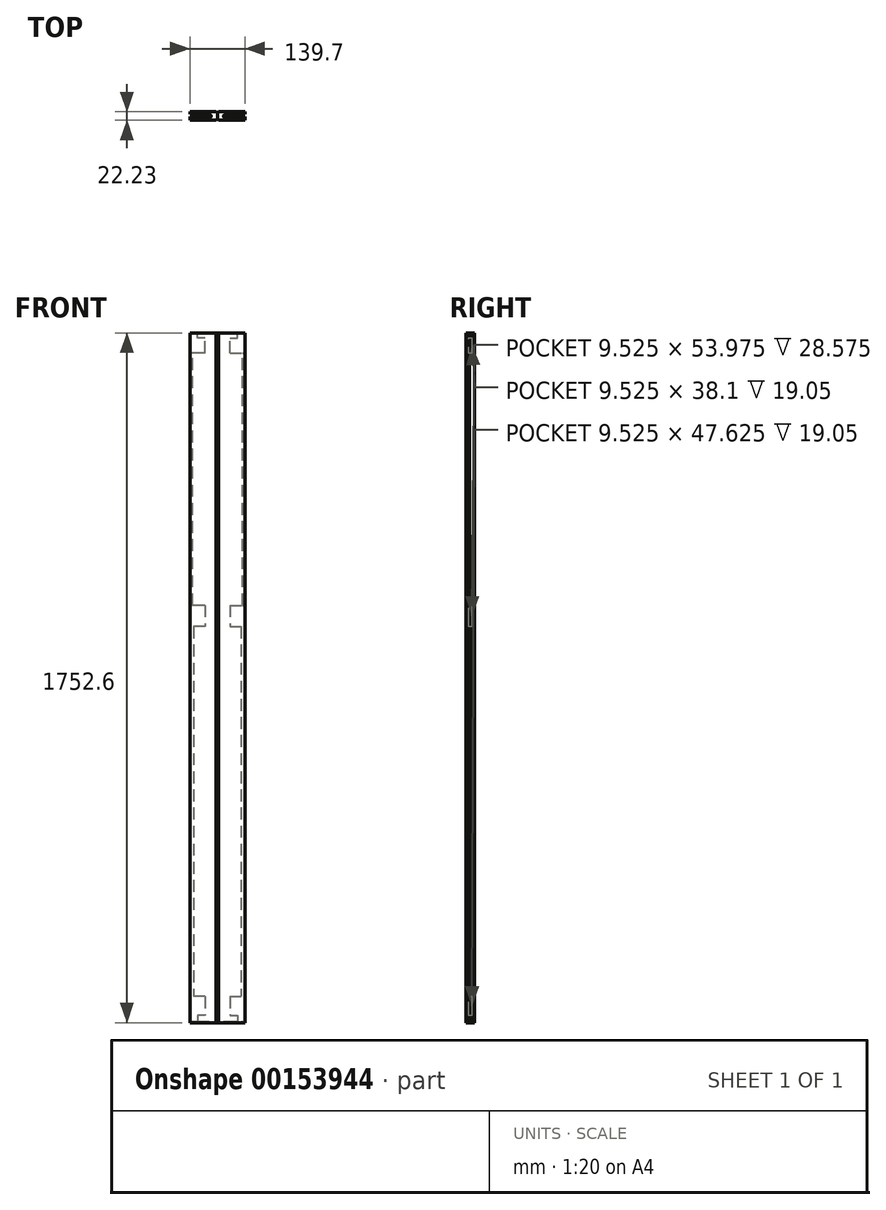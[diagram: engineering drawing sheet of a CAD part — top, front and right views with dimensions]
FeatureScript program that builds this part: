
annotation { "Feature Type Name" : "Feature", "Feature Type Description" : "" }
export const myFeature = defineFeature(function(context is Context, id is Id, definition is map)
    precondition{}
    {
        {
            var Q0;
            Q0=qCreatedBy(makeId("Front.planeOp"),FACE);
            var sketch = newSketch(context, id + "F0", { "sketchPlane" : qUnion([Q0])});
            skLineSegment(sketch, "E0.bottom", {"start": v(0, 0) * mm, "end": v(69.85, 0) * mm});
            skLineSegment(sketch, "E0.top", {"start": v(0, 1778) * mm, "end": v(69.85, 1778) * mm});
            skLineSegment(sketch, "E0.left", {"start": v(0, 0) * mm, "end": v(0, 1778) * mm});
            skLineSegment(sketch, "E0.right", {"start": v(69.85, 0) * mm, "end": v(69.85, 1778) * mm});
            skSolve(sketch);
        }
        {
            var Q0;
            Q0=makeQuery(id+"F0.imprint","IMPRINT",FACE,{"disambiguationData":[TD([[makeQuery(id+"F0.imprint","IMPRINT",EDGE,{"derivedFrom":sQuery(id+"F0.wireOp",EDGE,"E0.bottom")}),1.0]])]});
            extrude(context, id + "F1", {"entities" : qUnion([Q0]), "depth" : 22.22 * mm});
        }
        {
            var Q0;
            Q0=makeQuery(id+"F1.opExtrude","SWEPT_FACE",FACE,{"disambiguationData":[OSD([sQuery(id+"F0.wireOp",EDGE,"E0.right")])]});
            var sketch = newSketch(context, id + "F2", { "sketchPlane" : qUnion([Q0])});
            skLineSegment(sketch, "E1.bottom", {"start": v(-15.87, 79.37) * mm, "end": v(-6.35, 79.37) * mm});
            skLineSegment(sketch, "E1.top", {"start": v(-15.87, 0) * mm, "end": v(-6.35, 0) * mm});
            skLineSegment(sketch, "E1.left", {"start": v(-15.88, 79.37) * mm, "end": v(-15.87, 0) * mm});
            skLineSegment(sketch, "E1.right", {"start": v(-6.35, 79.37) * mm, "end": v(-6.35, 0) * mm});
            skLineSegment(sketch, "E2.bottom", {"start": v(-22.23, 88.9) * mm, "end": v(0, 88.9) * mm, "construction": true});
            skLineSegment(sketch, "E2.top", {"start": v(-22.23, 0) * mm, "end": v(0, 0) * mm, "construction": true});
            skLineSegment(sketch, "E2.left", {"start": v(-22.23, 88.9) * mm, "end": v(-22.23, 0) * mm, "construction": true});
            skLineSegment(sketch, "E2.right", {"start": v(0, 88.9) * mm, "end": v(0, 0) * mm, "construction": true});
            skLineSegment(sketch, "E3", {"start": v(-15.88, 31.75) * mm, "end": v(-6.35, 31.75) * mm});
            skLineSegment(sketch, "E4.bottom", {"start": v(-15.88, 1714.5) * mm, "end": v(-6.35, 1714.5) * mm});
            skLineSegment(sketch, "E4.top", {"start": v(-15.88, 1778) * mm, "end": v(-6.35, 1778) * mm});
            skLineSegment(sketch, "E4.left", {"start": v(-15.88, 1714.5) * mm, "end": v(-15.88, 1778) * mm});
            skLineSegment(sketch, "E4.right", {"start": v(-6.35, 1714.5) * mm, "end": v(-6.35, 1778) * mm});
            skLineSegment(sketch, "E5.bottom", {"start": v(0, 1778) * mm, "end": v(-22.23, 1778) * mm, "construction": true});
            skLineSegment(sketch, "E5.top", {"start": v(0, 1689.1) * mm, "end": v(-22.23, 1689.1) * mm, "construction": true});
            skLineSegment(sketch, "E5.left", {"start": v(0, 1778) * mm, "end": v(0, 1689.1) * mm, "construction": true});
            skLineSegment(sketch, "E5.right", {"start": v(-22.23, 1778) * mm, "end": v(-22.23, 1689.1) * mm, "construction": true});
            skLineSegment(sketch, "E6", {"start": v(-15.88, 1752.6) * mm, "end": v(-6.35, 1752.6) * mm});
            skLineSegment(sketch, "E7.bottom", {"start": v(-6.35, 1073.15) * mm, "end": v(-15.88, 1073.15) * mm});
            skLineSegment(sketch, "E7.top", {"start": v(-6.35, 1019.18) * mm, "end": v(-15.88, 1019.18) * mm});
            skLineSegment(sketch, "E7.left", {"start": v(-6.35, 1073.15) * mm, "end": v(-6.35, 1019.18) * mm});
            skLineSegment(sketch, "E7.right", {"start": v(-15.88, 1073.15) * mm, "end": v(-15.88, 1019.18) * mm});
            skLineSegment(sketch, "E8.bottom", {"start": v(-22.23, 1098.55) * mm, "end": v(0, 1098.55) * mm, "construction": true});
            skLineSegment(sketch, "E8.top", {"start": v(-22.23, 993.78) * mm, "end": v(0, 993.78) * mm, "construction": true});
            skLineSegment(sketch, "E8.left", {"start": v(-22.23, 1098.55) * mm, "end": v(-22.23, 993.78) * mm, "construction": true});
            skLineSegment(sketch, "E8.right", {"start": v(0, 1098.55) * mm, "end": v(0, 993.78) * mm, "construction": true});
            skSolve(sketch);
        }
        {
            var Q0;
            {var subQ0=sQuery(id+"F2.wireOp",EDGE,"E1.bottom");Q0=makeQuery(id+"F2.imprint","IMPRINT",FACE,{"disambiguationData":[TD([[makeQuery(id+"F2.imprint","IMPRINT",EDGE,{"derivedFrom":subQ0}),-1.0]])]});}
            var Q1;
            {var subQ0=sQuery(id+"F2.wireOp",EDGE,"E4.bottom");Q1=makeQuery(id+"F2.imprint","IMPRINT",FACE,{"disambiguationData":[TD([[makeQuery(id+"F2.imprint","IMPRINT",EDGE,{"derivedFrom":subQ0}),1.0]])]});}
            var Q2;
            Q2=makeQuery(id+"F2.imprint","IMPRINT",FACE,{"disambiguationData":[TD([[makeQuery(id+"F2.imprint","IMPRINT",EDGE,{"derivedFrom":sQuery(id+"F2.wireOp",EDGE,"E7.bottom")}),1.0]])]});
            extrude(context, id + "F3", {"entities" : qUnion([Q0, Q1, Q2]), "operationType" : NewBodyOperationType.REMOVE, "oppositeDirection" : true, "depth" : 38.1 * mm});
        }
        {
            var Q0;
            {var subQ0=sQuery(id+"F2.wireOp",EDGE,"E1.top");Q0=makeQuery(id+"F2.imprint","IMPRINT",FACE,{"disambiguationData":[TD([[makeQuery(id+"F2.imprint","IMPRINT",EDGE,{"derivedFrom":subQ0}),1.0]])]});}
            var Q1;
            {var subQ0=sQuery(id+"F2.wireOp",EDGE,"E4.top");Q1=makeQuery(id+"F2.imprint","IMPRINT",FACE,{"disambiguationData":[TD([[makeQuery(id+"F2.imprint","IMPRINT",EDGE,{"derivedFrom":subQ0}),-1.0]])]});}
            extrude(context, id + "F4", {"entities" : qUnion([Q0, Q1]), "operationType" : NewBodyOperationType.REMOVE, "oppositeDirection" : true, "depth" : 19.05 * mm});
        }
        {
            var Q0;
            Q0=makeQuery(id+"F1.opExtrude","CAP_FACE",FACE,{"disambiguationData":[OSD([sQuery(id+"F0.wireOp",EDGE,"E0.bottom"),sQuery(id+"F0.wireOp",EDGE,"E0.top"),sQuery(id+"F0.wireOp",EDGE,"E0.left"),sQuery(id+"F0.wireOp",EDGE,"E0.right")])],"isStart":false});
            var sketch = newSketch(context, id + "F5", { "sketchPlane" : qUnion([Q0])});
            skLineSegment(sketch, "E9", {"start": v(0, 1765.3) * mm, "end": v(69.85, 1765.3) * mm});
            skLineSegment(sketch, "E10", {"start": v(0, 12.7) * mm, "end": v(69.85, 12.7) * mm});
            skSolve(sketch);
        }
        {
            var Q0;
            {var subQ0=sQuery(id+"F5.wireOp",EDGE,"E10");Q0=makeQuery(id+"F5.imprint","IMPRINT",FACE,{"disambiguationData":[TD([[makeQuery(id+"F5.imprint","IMPRINT",EDGE,{"derivedFrom":subQ0}),-1.0]])]});}
            var Q1;
            {var subQ0=sQuery(id+"F5.wireOp",EDGE,"E9");Q1=makeQuery(id+"F5.imprint","IMPRINT",FACE,{"disambiguationData":[TD([[makeQuery(id+"F5.imprint","IMPRINT",EDGE,{"derivedFrom":subQ0}),1.0]])]});}
            extrude(context, id + "F6", {"entities" : qUnion([Q0, Q1]), "operationType" : NewBodyOperationType.REMOVE, "endBound" : BoundingType.THROUGH_ALL, "oppositeDirection" : true, "depth" : 25.4 * mm});
        }
        {
            var Q0;
            Q0=makeQuery(id+"F1.opExtrude","SWEPT_FACE",FACE,{"disambiguationData":[OSD([sQuery(id+"F0.wireOp",EDGE,"E0.right")])]});
            var sketch = newSketch(context, id + "F7", { "sketchPlane" : qUnion([Q0])});
            skLineSegment(sketch, "E11.bottom", {"start": v(-15.88, 79.37) * mm, "end": v(-6.35, 79.37) * mm});
            skLineSegment(sketch, "E11.top", {"start": v(-15.88, 1019.18) * mm, "end": v(-6.35, 1019.18) * mm});
            skLineSegment(sketch, "E11.left", {"start": v(-15.88, 79.37) * mm, "end": v(-15.88, 1019.18) * mm});
            skLineSegment(sketch, "E11.right", {"start": v(-6.35, 79.37) * mm, "end": v(-6.35, 1019.18) * mm});
            skLineSegment(sketch, "E12.bottom", {"start": v(0, 1073.15) * mm, "end": v(-12.7, 1073.15) * mm});
            skLineSegment(sketch, "E12.top", {"start": v(0, 1714.5) * mm, "end": v(-12.7, 1714.5) * mm});
            skLineSegment(sketch, "E12.left", {"start": v(0, 1073.15) * mm, "end": v(0, 1714.5) * mm});
            skLineSegment(sketch, "E12.right", {"start": v(-12.7, 1073.15) * mm, "end": v(-12.7, 1714.5) * mm});
            skSolve(sketch);
        }
        {
            var Q0;
            {var subQ0=sQuery(id+"F7.wireOp",EDGE,"E11.top");Q0=makeQuery(id+"F7.imprint","IMPRINT",FACE,{"disambiguationData":[TD([[makeQuery(id+"F7.imprint","IMPRINT",EDGE,{"derivedFrom":subQ0}),-1.0]])]});}
            var Q1;
            {var subQ0=sQuery(id+"F7.wireOp",EDGE,"E11.bottom");Q1=makeQuery(id+"F7.imprint","IMPRINT",FACE,{"disambiguationData":[TD([[makeQuery(id+"F7.imprint","IMPRINT",EDGE,{"derivedFrom":subQ0}),1.0]])]});}
            extrude(context, id + "F8", {"entities" : qUnion([Q0, Q1]), "operationType" : NewBodyOperationType.REMOVE, "oppositeDirection" : true, "depth" : 9.52 * mm});
        }
        {
            var Q0;
            Q0=makeQuery(id+"F6.boolean.opBoolean","COPY",FACE,{"derivedFrom":makeQuery(id+"F6.opExtrude","SWEPT_FACE",FACE,{"disambiguationData":[OSD([sQuery(id+"F5.wireOp",EDGE,"E10")])]})});
            var sketch = newSketch(context, id + "F9", { "sketchPlane" : qUnion([Q0])});
            skArc(sketch, "E13", {"start": v(20.64, 16.67) * mm, "mid": v(15.88, 11.9) * mm, "end": v(20.64, 7.14) * mm});
            skArc(sketch, "E14", {"start": v(61.91, 7.14) * mm, "mid": v(66.67, 11.9) * mm, "end": v(61.91, 16.67) * mm});
            skLineSegment(sketch, "E15", {"start": v(20.64, 16.67) * mm, "end": v(61.91, 16.67) * mm});
            skLineSegment(sketch, "E16", {"start": v(61.91, 7.14) * mm, "end": v(20.64, 7.14) * mm});
            skLineSegment(sketch, "E17", {"start": v(20.64, 11.9) * mm, "end": v(61.91, 11.9) * mm, "construction": true});
            skSolve(sketch);
        }
        {
            var Q0;
            Q0=makeQuery(id+"F6.boolean.opBoolean","COPY",FACE,{"derivedFrom":makeQuery(id+"F6.opExtrude","SWEPT_FACE",FACE,{"disambiguationData":[OSD([sQuery(id+"F5.wireOp",EDGE,"E9")])]})});
            var sketch = newSketch(context, id + "F10", { "sketchPlane" : qUnion([Q0])});
            skArc(sketch, "E18", {"start": v(20.64, -7.14) * mm, "mid": v(15.88, -11.9) * mm, "end": v(20.64, -16.67) * mm});
            skLineSegment(sketch, "E19", {"start": v(20.64, -7.14) * mm, "end": v(61.91, -7.14) * mm});
            skArc(sketch, "E20", {"start": v(61.91, -16.67) * mm, "mid": v(66.67, -11.9) * mm, "end": v(61.91, -7.14) * mm});
            skLineSegment(sketch, "E21", {"start": v(20.64, -16.67) * mm, "end": v(61.91, -16.67) * mm});
            skSolve(sketch);
        }
        {
            var Q0;
            {var subQ5=sQuery(id+"F9.wireOp",EDGE,"E15");Q0=makeQuery(id+"F9.imprint","IMPRINT",FACE,{"disambiguationData":[TD([[makeQuery(id+"F9.imprint","IMPRINT",EDGE,{"derivedFrom":subQ5}),-1.0]])]});}
            var Q1;
            {var subQ0=sQuery(id+"F9.wireOp",EDGE,"E16");var subQ1=sQuery(id+"F9.wireOp",EDGE,"E14");var subQ2=makeQuery(id+"F9.imprint","INTERSECT",VERTEX,{"derivedFrom":[subQ1,subQ0]});Q1=makeQuery(id+"F9.imprint","IMPRINT",FACE,{"disambiguationData":[TD([[makeQuery(id+"F9.imprint","IMPRINT",EDGE,{"disambiguationData":[TD([[subQ2,-1.0]])],"derivedFrom":subQ1}),1.0]])]});}
            extrude(context, id + "F11", {"entities" : qUnion([Q0, Q1]), "operationType" : NewBodyOperationType.REMOVE, "oppositeDirection" : true, "depth" : 1.98 * mm});
        }
        {
            var Q0;
            {var subQ7=sQuery(id+"F10.wireOp",EDGE,"E18");Q0=makeQuery(id+"F10.imprint","IMPRINT",FACE,{"disambiguationData":[TD([[makeQuery(id+"F10.imprint","IMPRINT",EDGE,{"derivedFrom":subQ7}),1.0]])]});}
            var Q1;
            {var subQ0=sQuery(id+"F10.wireOp",EDGE,"E20");var subQ1=sQuery(id+"F10.wireOp",EDGE,"E19");var subQ2=makeQuery(id+"F10.imprint","INTERSECT",VERTEX,{"derivedFrom":[subQ1,subQ0]});Q1=makeQuery(id+"F10.imprint","IMPRINT",FACE,{"disambiguationData":[TD([[makeQuery(id+"F10.imprint","IMPRINT",EDGE,{"disambiguationData":[TD([[subQ2,1.0]])],"derivedFrom":subQ0}),1.0]])]});}
            extrude(context, id + "F12", {"entities" : qUnion([Q0, Q1]), "operationType" : NewBodyOperationType.REMOVE, "oppositeDirection" : true, "depth" : 1.98 * mm});
        }
        {
            var Q0;
            Q0=makeQuery(id+"F1.opExtrude","CAP_EDGE",EDGE,{"disambiguationData":[OSD([sQuery(id+"F0.wireOp",EDGE,"E0.left")])],"isStart":false});
            var Q1;
            Q1=makeQuery(id+"F1.opExtrude","CAP_EDGE",EDGE,{"disambiguationData":[OSD([sQuery(id+"F0.wireOp",EDGE,"E0.left")])],"isStart":true});
            chamfer(context, id + "F13", {"entities" : qUnion([Q0, Q1]), "width" : 3.17 * mm, "tangentPropagation" : true});
        }
        {
            var Q0;
            {var subQ3=sQuery(id+"F7.wireOp",EDGE,"E12.left");Q0=makeQuery(id+"F7.imprint","IMPRINT",FACE,{"disambiguationData":[TD([[makeQuery(id+"F7.imprint","IMPRINT",EDGE,{"derivedFrom":subQ3}),1.0]])]});}
            extrude(context, id + "F14", {"entities" : qUnion([Q0]), "operationType" : NewBodyOperationType.REMOVE, "oppositeDirection" : true, "depth" : 6.35 * mm});
        }
        {
            var Q0;
            Q0=makeQuery(id+"F1.opExtrude","SWEPT_BODY",BODY,{"disambiguationData":[OSD([sQuery(id+"F0.wireOp",EDGE,"E0.bottom"),sQuery(id+"F0.wireOp",EDGE,"E0.top"),sQuery(id+"F0.wireOp",EDGE,"E0.left"),sQuery(id+"F0.wireOp",EDGE,"E0.right")])]});
            var Q1;
            Q1=qCreatedBy(makeId("Right.planeOp"),FACE);
            mirror(context, id + "F15", {"entities" : qUnion([Q0]), "mirrorPlane" : qUnion([Q1])});
        }
    });
